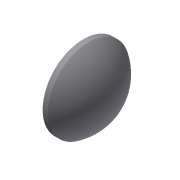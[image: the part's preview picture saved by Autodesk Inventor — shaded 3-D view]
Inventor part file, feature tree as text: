
AUTODESK INVENTOR PART (.ipt)
format: ipt  version: 2019.4 (Build 234330000, 330)  size: 98,304 bytes
history: native  units: mm
features: revolve x1, sketch x1
ambient origin geometry x8: Origin, YZ Plane, XZ Plane, XY Plane, X Axis, Y Axis, Z Axis, Center Point
bodies: Solid1 (feature_tree)
feature tree (2):
  revolve  "Revolution1"  [1 undecoded]
  sketch  "Sketch1"  dims[d0=8.1mm d1=2.8mm d2=7.86mm d3=1.0mm d4=90.0deg]
note: 1 required parameter value undecoded (feature->parameter linkage not recoverable at this tier; creation-order binding heuristic only, values carry confidence <= 0.55)
